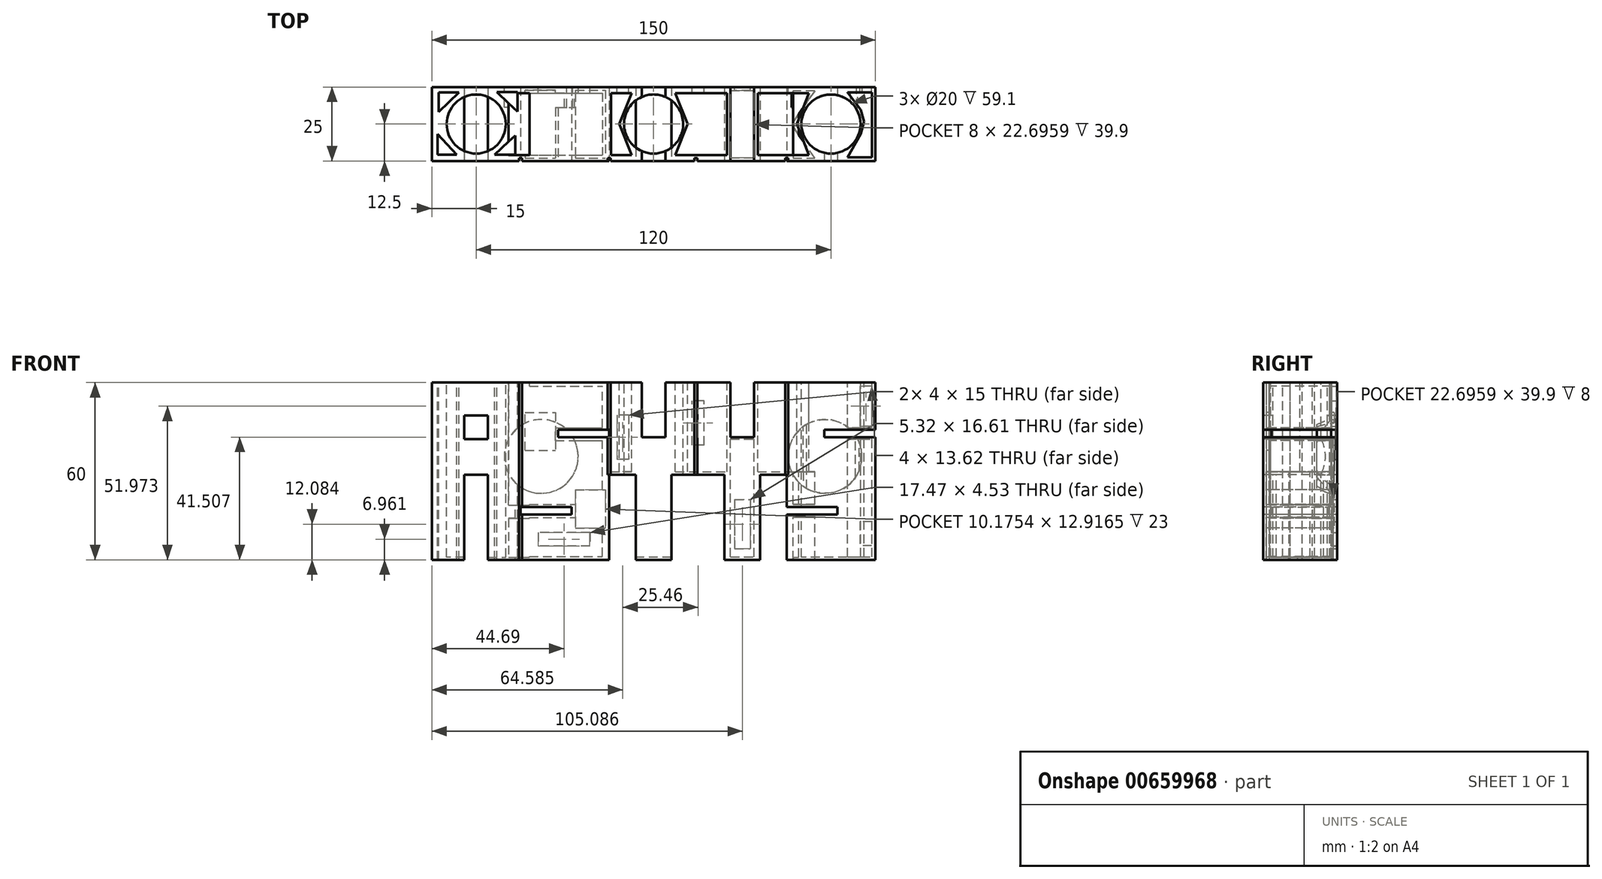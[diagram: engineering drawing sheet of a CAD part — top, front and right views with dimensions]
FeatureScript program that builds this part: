
annotation { "Feature Type Name" : "Feature", "Feature Type Description" : "" }
export const myFeature = defineFeature(function(context is Context, id is Id, definition is map)
    precondition{}
    {
        {
            var Q0;
            Q0=qCreatedBy(makeId("Front.planeOp"),FACE);
            var sketch = newSketch(context, id + "F0", { "sketchPlane" : qUnion([Q0])});
            skLineSegment(sketch, "E0.bottom", {"start": v(-75, 38.6) * mm, "end": v(75, 38.6) * mm});
            skLineSegment(sketch, "E0.top", {"start": v(-75, -21.4) * mm, "end": v(75, -21.4) * mm});
            skLineSegment(sketch, "E0.left", {"start": v(-75, 38.6) * mm, "end": v(-75, -21.4) * mm});
            skLineSegment(sketch, "E0.right", {"start": v(75, 38.6) * mm, "end": v(75, -21.4) * mm});
            skSolve(sketch);
        }
        {
            var Q0;
            Q0=qSketchRegion(id+"F0",true);
            extrude(context, id + "F1", {"entities" : qUnion([Q0]), "depth" : 25 * mm, "offsetDistance" : 25 * mm});
        }
        {
            var Q0;
            Q0=makeQuery(id+"F1.opExtrude","SWEPT_FACE",FACE,{"disambiguationData":[OSD([sQuery(id+"F0.wireOp",EDGE,"E0.bottom")])]});
            var sketch = newSketch(context, id + "F2", { "sketchPlane" : qUnion([Q0])});
            skLineSegment(sketch, "E1.bottom", {"start": v(-73, -2) * mm, "end": v(73, -2) * mm});
            skLineSegment(sketch, "E1.top", {"start": v(-73, -23) * mm, "end": v(73, -23) * mm});
            skLineSegment(sketch, "E1.left", {"start": v(-73, -2) * mm, "end": v(-73, -23) * mm});
            skLineSegment(sketch, "E1.right", {"start": v(73, -2) * mm, "end": v(73, -23) * mm});
            skLineSegment(sketch, "E2.MirrorCS", {"start": v(219, -2) * mm, "end": v(219, -23) * mm});
            skSolve(sketch);
        }
        {
            var Q0;
            Q0=qSketchRegion(id+"F2",true);
            extrude(context, id + "F3", {"entities" : qUnion([Q0]), "operationType" : NewBodyOperationType.ADD, "oppositeDirection" : true, "depth" : 2 * mm, "offsetDistance" : 25 * mm});
        }
        {
            var Q0;
            Q0=makeQuery(id+"F3.boolean.opBoolean","MERGE",FACE,{"derivedFrom":[makeQuery(id+"F1.opExtrude","SWEPT_FACE",FACE,{"disambiguationData":[OSD([sQuery(id+"F0.wireOp",EDGE,"E0.bottom")])]}),makeQuery(id+"F3.opExtrude","CAP_FACE",FACE,{"disambiguationData":[OSD([sQuery(id+"F2.wireOp",EDGE,"E1.bottom"),sQuery(id+"F2.wireOp",EDGE,"E1.top"),sQuery(id+"F2.wireOp",EDGE,"E1.left"),sQuery(id+"F2.wireOp",EDGE,"E1.right")])],"isStart":true})]});
            var sketch = newSketch(context, id + "F4", { "sketchPlane" : qUnion([Q0])});
            skCircle(sketch, "E3", {"center": v(60, -12.5) * mm, "radius": 10 * mm});
            skCircle(sketch, "E4.MirrorC", {"center": v(-60, -12.5) * mm, "radius": 10 * mm});
            skCircle(sketch, "E5", {"center": v(0, -12.5) * mm, "radius": 10 * mm});
            skSolve(sketch);
        }
        {
            var Q0;
            Q0=qSketchRegion(id+"F4",true);
            extrude(context, id + "F5", {"entities" : qUnion([Q0]), "operationType" : NewBodyOperationType.REMOVE, "oppositeDirection" : true, "depth" : 59.1 * mm, "offsetDistance" : 25 * mm});
        }
        {
            var Q0;
            Q0=makeQuery(id+"F1.opExtrude","CAP_FACE",FACE,{"disambiguationData":[OSD([sQuery(id+"F0.wireOp",EDGE,"E0.bottom"),sQuery(id+"F0.wireOp",EDGE,"E0.top"),sQuery(id+"F0.wireOp",EDGE,"E0.left"),sQuery(id+"F0.wireOp",EDGE,"E0.right")])],"isStart":true});
            var sketch = newSketch(context, id + "F6", { "sketchPlane" : qUnion([Q0])});
            skCircle(sketch, "E6", {"center": v(-58, 13.6) * mm, "radius": 12.5 * mm});
            skCircle(sketch, "E7.MirrorC", {"center": v(38, 13.6) * mm, "radius": 12.5 * mm});
            skSolve(sketch);
        }
        {
            var Q0;
            Q0=qSketchRegion(id+"F6",true);
            extrude(context, id + "F7", {"entities" : qUnion([Q0]), "operationType" : NewBodyOperationType.REMOVE, "oppositeDirection" : true, "depth" : 6.9 * mm, "offsetDistance" : 25 * mm});
        }
        {
            var Q0;
            Q0=makeQuery(id+"F1.opExtrude","CAP_FACE",FACE,{"disambiguationData":[OSD([sQuery(id+"F0.wireOp",EDGE,"E0.bottom"),sQuery(id+"F0.wireOp",EDGE,"E0.top"),sQuery(id+"F0.wireOp",EDGE,"E0.left"),sQuery(id+"F0.wireOp",EDGE,"E0.right")])],"isStart":false});
            var sketch = newSketch(context, id + "F8", { "sketchPlane" : qUnion([Q0])});
            skLineSegment(sketch, "E8.bottom", {"start": v(-75, 38.6) * mm, "end": v(-45, 38.6) * mm});
            skLineSegment(sketch, "E8.top", {"start": v(-75, -21.4) * mm, "end": v(-45, -21.4) * mm});
            skLineSegment(sketch, "E8.left", {"start": v(-75, 38.6) * mm, "end": v(-75, -21.4) * mm});
            skLineSegment(sketch, "E8.right", {"start": v(-45, 38.6) * mm, "end": v(-45, -21.4) * mm});
            skLineSegment(sketch, "E9", {"start": v(-60, 38.6) * mm, "end": v(-60, -21.4) * mm});
            skLineSegment(sketch, "E10", {"start": v(-64, -21.4) * mm, "end": v(-64, 7.4) * mm});
            skLineSegment(sketch, "E11", {"start": v(-64, 7.4) * mm, "end": v(-60, 7.4) * mm});
            skLineSegment(sketch, "E12", {"start": v(-60, 27.44) * mm, "end": v(-64, 27.44) * mm});
            skLineSegment(sketch, "E13", {"start": v(-64, 27.44) * mm, "end": v(-64, 19.44) * mm});
            skLineSegment(sketch, "E14", {"start": v(-64, 19.44) * mm, "end": v(-60, 19.44) * mm});
            skLineSegment(sketch, "E15.MirrorCS", {"start": v(-60, 27.44) * mm, "end": v(-56, 27.44) * mm});
            skLineSegment(sketch, "E16.MirrorCS", {"start": v(-56, 27.44) * mm, "end": v(-56, 19.44) * mm});
            skLineSegment(sketch, "E17.MirrorCS", {"start": v(-56, 19.44) * mm, "end": v(-60, 19.44) * mm});
            skLineSegment(sketch, "E18.MirrorCS", {"start": v(-56, 7.4) * mm, "end": v(-60, 7.4) * mm});
            skLineSegment(sketch, "E19.MirrorCS", {"start": v(-56, -21.4) * mm, "end": v(-56, 7.4) * mm});
            skLineSegment(sketch, "E20.bottom", {"start": v(-45, 38.6) * mm, "end": v(-15, 38.6) * mm});
            skLineSegment(sketch, "E20.top", {"start": v(-45, -21.4) * mm, "end": v(-15, -21.4) * mm});
            skLineSegment(sketch, "E20.right", {"start": v(-15, 38.6) * mm, "end": v(-15, -21.4) * mm});
            skLineSegment(sketch, "E21.bottom", {"start": v(-15, 20.1) * mm, "end": v(-32.25, 20.1) * mm});
            skLineSegment(sketch, "E21.top", {"start": v(-15, 22.68) * mm, "end": v(-32.25, 22.68) * mm});
            skLineSegment(sketch, "E21.left", {"start": v(-15, 22.68) * mm, "end": v(-15, 20.1) * mm});
            skLineSegment(sketch, "E21.right", {"start": v(-32.25, 22.68) * mm, "end": v(-32.25, 20.1) * mm});
            skLineSegment(sketch, "E22.bottom", {"start": v(-45, -3.49) * mm, "end": v(-27.75, -3.49) * mm});
            skLineSegment(sketch, "E22.top", {"start": v(-45, -6.06) * mm, "end": v(-27.75, -6.06) * mm});
            skLineSegment(sketch, "E22.left", {"start": v(-45, -3.49) * mm, "end": v(-45, -6.06) * mm});
            skLineSegment(sketch, "E22.right", {"start": v(-27.75, -3.49) * mm, "end": v(-27.75, -6.06) * mm});
            skLineSegment(sketch, "E23.bottom", {"start": v(-15, 38.6) * mm, "end": v(15, 38.6) * mm});
            skLineSegment(sketch, "E23.top", {"start": v(-15, -21.4) * mm, "end": v(15, -21.4) * mm});
            skLineSegment(sketch, "E23.right", {"start": v(15, 38.6) * mm, "end": v(15, -21.4) * mm});
            skLineSegment(sketch, "E24", {"start": v(-4, 38.6) * mm, "end": v(-4, 20.1) * mm});
            skLineSegment(sketch, "E25", {"start": v(-4, 20.1) * mm, "end": v(0, 20.1) * mm});
            skLineSegment(sketch, "E26.MirrorCS", {"start": v(4, 38.6) * mm, "end": v(4, 20.1) * mm});
            skLineSegment(sketch, "E27.MirrorCS", {"start": v(4, 20.1) * mm, "end": v(0, 20.1) * mm});
            skLineSegment(sketch, "E28", {"start": v(-15, 7.4) * mm, "end": v(-6, 7.4) * mm});
            skLineSegment(sketch, "E29", {"start": v(-6, 7.4) * mm, "end": v(-6, -21.4) * mm});
            skLineSegment(sketch, "E30.bottom", {"start": v(15, 38.6) * mm, "end": v(45, 38.6) * mm});
            skLineSegment(sketch, "E30.top", {"start": v(15, -21.4) * mm, "end": v(45, -21.4) * mm});
            skLineSegment(sketch, "E30.right", {"start": v(45, 38.6) * mm, "end": v(45, -21.4) * mm});
            skLineSegment(sketch, "E31", {"start": v(30, 38.6) * mm, "end": v(30, -21.4) * mm});
            skLineSegment(sketch, "E32", {"start": v(26, 20.1) * mm, "end": v(30, 20.1) * mm});
            skLineSegment(sketch, "E33", {"start": v(26, 20.1) * mm, "end": v(26, 38.6) * mm});
            skLineSegment(sketch, "E34.MirrorCS", {"start": v(34, 20.1) * mm, "end": v(34, 38.6) * mm});
            skLineSegment(sketch, "E35.MirrorCS", {"start": v(34, 20.1) * mm, "end": v(30, 20.1) * mm});
            skLineSegment(sketch, "E36", {"start": v(15, 7.4) * mm, "end": v(24, 7.4) * mm});
            skLineSegment(sketch, "E37", {"start": v(24, 7.4) * mm, "end": v(24, -21.4) * mm});
            skLineSegment(sketch, "E38.MirrorCS", {"start": v(45, 7.4) * mm, "end": v(36, 7.4) * mm});
            skLineSegment(sketch, "E39.MirrorCS", {"start": v(36, 7.4) * mm, "end": v(36, -21.4) * mm});
            skLineSegment(sketch, "E40.MirrorCS", {"start": v(6, 7.4) * mm, "end": v(6, -21.4) * mm});
            skLineSegment(sketch, "E41", {"start": v(6, 7.4) * mm, "end": v(15, 7.4) * mm});
            skLineSegment(sketch, "E42", {"start": v(57.75, 22.68) * mm, "end": v(75, 22.68) * mm});
            skLineSegment(sketch, "E43", {"start": v(57.75, 20.1) * mm, "end": v(75, 20.1) * mm});
            skPoint(sketch, "E43.startSnap0", {"position": v(32, 20.1) * mm});
            skLineSegment(sketch, "E44", {"start": v(57.75, 22.68) * mm, "end": v(57.75, 20.1) * mm});
            skLineSegment(sketch, "E45", {"start": v(45, -3.49) * mm, "end": v(62.25, -3.49) * mm});
            skLineSegment(sketch, "E46", {"start": v(62.25, -3.49) * mm, "end": v(62.25, -6.06) * mm});
            skLineSegment(sketch, "E47", {"start": v(62.25, -6.06) * mm, "end": v(45, -6.06) * mm});
            skSolve(sketch);
        }
        {
            var Q0;
            {var subQ0=sQuery(id+"F8.wireOp",EDGE,"E12");Q0=makeQuery(id+"F8.imprint","IMPRINT",FACE,{"disambiguationData":[TD([[makeQuery(id+"F8.imprint","IMPRINT",EDGE,{"derivedFrom":subQ0}),1.0]])]});}
            var Q1;
            {var subQ0=sQuery(id+"F8.wireOp",EDGE,"E15.MirrorCS");Q1=makeQuery(id+"F8.imprint","IMPRINT",FACE,{"disambiguationData":[TD([[makeQuery(id+"F8.imprint","IMPRINT",EDGE,{"derivedFrom":subQ0}),-1.0]])]});}
            var Q2;
            {var subQ3=sQuery(id+"F8.wireOp",EDGE,"E10");Q2=makeQuery(id+"F8.imprint","IMPRINT",FACE,{"disambiguationData":[TD([[makeQuery(id+"F8.imprint","IMPRINT",EDGE,{"derivedFrom":subQ3}),-1.0]])]});}
            var Q3;
            {var subQ4=sQuery(id+"F8.wireOp",EDGE,"E18.MirrorCS");Q3=makeQuery(id+"F8.imprint","IMPRINT",FACE,{"disambiguationData":[TD([[makeQuery(id+"F8.imprint","IMPRINT",EDGE,{"derivedFrom":subQ4}),1.0]])]});}
            var Q4;
            Q4=makeQuery(id+"F8.imprint","IMPRINT",FACE,{"disambiguationData":[TD([[makeQuery(id+"F8.imprint","IMPRINT",EDGE,{"derivedFrom":sQuery(id+"F8.wireOp",EDGE,"E22.bottom")}),-1.0]])]});
            var Q5;
            {var subQ0=sQuery(id+"F8.wireOp",EDGE,"E21.bottom");Q5=makeQuery(id+"F8.imprint","IMPRINT",FACE,{"disambiguationData":[TD([[makeQuery(id+"F8.imprint","IMPRINT",EDGE,{"derivedFrom":subQ0}),-1.0]])]});}
            var Q6;
            {var subQ1=sQuery(id+"F8.wireOp",EDGE,"E24");Q6=makeQuery(id+"F8.imprint","IMPRINT",FACE,{"disambiguationData":[TD([[makeQuery(id+"F8.imprint","IMPRINT",EDGE,{"derivedFrom":subQ1}),1.0]])]});}
            var Q7;
            {var subQ4=sQuery(id+"F8.wireOp",EDGE,"E28");Q7=makeQuery(id+"F8.imprint","IMPRINT",FACE,{"disambiguationData":[TD([[makeQuery(id+"F8.imprint","IMPRINT",EDGE,{"derivedFrom":subQ4}),-1.0]])]});}
            var Q8;
            {var subQ3=sQuery(id+"F8.wireOp",EDGE,"E40.MirrorCS");Q8=makeQuery(id+"F8.imprint","IMPRINT",FACE,{"disambiguationData":[TD([[makeQuery(id+"F8.imprint","IMPRINT",EDGE,{"derivedFrom":subQ3}),1.0]])]});}
            var Q9;
            {var subQ4=sQuery(id+"F8.wireOp",EDGE,"E36");Q9=makeQuery(id+"F8.imprint","IMPRINT",FACE,{"disambiguationData":[TD([[makeQuery(id+"F8.imprint","IMPRINT",EDGE,{"derivedFrom":subQ4}),-1.0]])]});}
            var Q10;
            {var subQ3=sQuery(id+"F8.wireOp",EDGE,"E34.MirrorCS");Q10=makeQuery(id+"F8.imprint","IMPRINT",FACE,{"disambiguationData":[TD([[makeQuery(id+"F8.imprint","IMPRINT",EDGE,{"derivedFrom":subQ3}),1.0]])]});}
            var Q11;
            {var subQ4=sQuery(id+"F8.wireOp",EDGE,"E32");Q11=makeQuery(id+"F8.imprint","IMPRINT",FACE,{"disambiguationData":[TD([[makeQuery(id+"F8.imprint","IMPRINT",EDGE,{"derivedFrom":subQ4}),1.0]])]});}
            var Q12;
            {var subQ4=sQuery(id+"F8.wireOp",EDGE,"E38.MirrorCS");Q12=makeQuery(id+"F8.imprint","IMPRINT",FACE,{"disambiguationData":[TD([[makeQuery(id+"F8.imprint","IMPRINT",EDGE,{"derivedFrom":subQ4}),1.0]])]});}
            var Q13;
            {var subQ0=sQuery(id+"F8.wireOp",EDGE,"E45");Q13=makeQuery(id+"F8.imprint","IMPRINT",FACE,{"disambiguationData":[TD([[makeQuery(id+"F8.imprint","IMPRINT",EDGE,{"derivedFrom":subQ0}),-1.0]])]});}
            var Q14;
            {var subQ0=sQuery(id+"F8.wireOp",EDGE,"E42");Q14=makeQuery(id+"F8.imprint","IMPRINT",FACE,{"disambiguationData":[TD([[makeQuery(id+"F8.imprint","IMPRINT",EDGE,{"derivedFrom":subQ0}),-1.0]])]});}
            extrude(context, id + "F9", {"entities" : qUnion([Q0, Q1, Q2, Q3, Q4, Q5, Q6, Q7, Q8, Q9, Q10, Q11, Q12, Q13, Q14]), "operationType" : NewBodyOperationType.REMOVE, "oppositeDirection" : true, "depth" : 35.6 * mm, "offsetDistance" : 25 * mm});
        }
        {
            var Q0;
            Q0=makeQuery(id+"F1.opExtrude","CAP_FACE",FACE,{"disambiguationData":[OSD([sQuery(id+"F0.wireOp",EDGE,"E0.bottom"),sQuery(id+"F0.wireOp",EDGE,"E0.top"),sQuery(id+"F0.wireOp",EDGE,"E0.left"),sQuery(id+"F0.wireOp",EDGE,"E0.right")])],"isStart":false});
            var sketch = newSketch(context, id + "F10", { "sketchPlane" : qUnion([Q0])});
            skPoint(sketch, "E48.oppositeSnap0", {"position": v(-45, -4.78) * mm});
            skLineSegment(sketch, "E48.bottom", {"start": v(-75, 38.6) * mm, "end": v(-45, 38.6) * mm});
            skLineSegment(sketch, "E48.top", {"start": v(-75, -21.4) * mm, "end": v(-45, -21.4) * mm});
            skLineSegment(sketch, "E48.left", {"start": v(-75, 38.6) * mm, "end": v(-75, -21.4) * mm});
            skLineSegment(sketch, "E48.right", {"start": v(-45, 38.6) * mm, "end": v(-45, -21.4) * mm});
            skLineSegment(sketch, "E49.bottom", {"start": v(-45, 38.6) * mm, "end": v(-15, 38.6) * mm});
            skLineSegment(sketch, "E49.top", {"start": v(-45, -21.4) * mm, "end": v(-15, -21.4) * mm});
            skLineSegment(sketch, "E49.right", {"start": v(-15, 38.6) * mm, "end": v(-15, -21.4) * mm});
            skLineSegment(sketch, "E50.bottom", {"start": v(-15, 38.6) * mm, "end": v(14.35, 38.6) * mm});
            skLineSegment(sketch, "E50.top", {"start": v(-15, -21.4) * mm, "end": v(14.35, -21.4) * mm});
            skLineSegment(sketch, "E50.right", {"start": v(14.35, 38.6) * mm, "end": v(14.35, -21.4) * mm});
            skLineSegment(sketch, "E51.bottom", {"start": v(14.35, 38.6) * mm, "end": v(45, 38.6) * mm});
            skLineSegment(sketch, "E51.top", {"start": v(14.35, -21.4) * mm, "end": v(45, -21.4) * mm});
            skLineSegment(sketch, "E51.right", {"start": v(45, 38.6) * mm, "end": v(45, -21.4) * mm});
            skLineSegment(sketch, "E52", {"start": v(-45.5, 38.6) * mm, "end": v(-45.5, -21.4) * mm});
            skLineSegment(sketch, "E53.MirrorCS", {"start": v(-44.5, 38.6) * mm, "end": v(-44.5, -21.4) * mm});
            skLineSegment(sketch, "E54", {"start": v(-14.5, 38.6) * mm, "end": v(-14.5, 7.4) * mm});
            skLineSegment(sketch, "E55", {"start": v(13.85, 38.6) * mm, "end": v(13.85, 7.4) * mm});
            skLineSegment(sketch, "E56.MirrorCS", {"start": v(14.85, 38.6) * mm, "end": v(14.85, 7.4) * mm});
            skLineSegment(sketch, "E57", {"start": v(44.5, 38.6) * mm, "end": v(44.5, 7.4) * mm});
            skLineSegment(sketch, "E58.MirrorCS", {"start": v(-15.5, 38.6) * mm, "end": v(-15.5, 7.4) * mm});
            skLineSegment(sketch, "E59", {"start": v(-15.5, 7.4) * mm, "end": v(-15, 7.4) * mm});
            skLineSegment(sketch, "E60.MirrorCS", {"start": v(45.5, 38.6) * mm, "end": v(45.5, 7.4) * mm});
            skLineSegment(sketch, "E61", {"start": v(45, 7.4) * mm, "end": v(45.5, 7.4) * mm});
            skSolve(sketch);
        }
        {
            var Q0;
            {var subQ1=makeQuery(id+"F9.boolean.opBoolean","COPY",EDGE,{"derivedFrom":makeQuery(id+"F9.opExtrude","CAP_EDGE",EDGE,{"disambiguationData":[OSD([sQuery(id+"F8.wireOp",EDGE,"E10")])],"isStart":true})});Q0=makeQuery(id+"F10.imprint","IMPRINT",FACE,{"disambiguationData":[TD([[makeQuery(id+"F10.imprint","IMPRINT",EDGE,{"derivedFrom":subQ1}),-1.0]])]});}
            var Q1;
            {var subQ1=makeQuery(id+"F9.boolean.opBoolean","COPY",EDGE,{"derivedFrom":makeQuery(id+"F9.opExtrude","CAP_EDGE",EDGE,{"disambiguationData":[OSD([sQuery(id+"F8.wireOp",EDGE,"E24")])],"isStart":true})});Q1=makeQuery(id+"F10.imprint","IMPRINT",FACE,{"disambiguationData":[TD([[makeQuery(id+"F10.imprint","IMPRINT",EDGE,{"derivedFrom":subQ1}),1.0]])]});}
            var Q2;
            {var subQ1=makeQuery(id+"F9.boolean.opBoolean","COPY",EDGE,{"derivedFrom":makeQuery(id+"F9.opExtrude","CAP_EDGE",EDGE,{"disambiguationData":[OSD([sQuery(id+"F8.wireOp",EDGE,"E33")])],"isStart":true})});Q2=makeQuery(id+"F10.imprint","IMPRINT",FACE,{"disambiguationData":[TD([[makeQuery(id+"F10.imprint","IMPRINT",EDGE,{"derivedFrom":subQ1}),-1.0]])]});}
            var Q3;
            Q3=makeQuery(id+"F10.imprint","IMPRINT",FACE,{"disambiguationData":[TD([[makeQuery(id+"F10.imprint","IMPRINT",EDGE,{"derivedFrom":makeQuery(id+"F9.boolean.opBoolean","COPY",EDGE,{"derivedFrom":makeQuery(id+"F9.opExtrude","CAP_EDGE",EDGE,{"disambiguationData":[OSD([sQuery(id+"F8.wireOp",EDGE,"E13")])],"isStart":true})})}),1.0]])]});
            var Q4;
            {var subQ1=sQuery(id+"F10.wireOp",EDGE,"E49.top");var subQ3=sQuery(id+"F10.wireOp",EDGE,"E53.MirrorCS");var subQ4=makeQuery(id+"F10.imprint","INTERSECT",VERTEX,{"derivedFrom":[subQ1,subQ3]});Q4=makeQuery(id+"F10.imprint","IMPRINT",FACE,{"disambiguationData":[TD([[makeQuery(id+"F10.imprint","IMPRINT",EDGE,{"disambiguationData":[TD([[subQ4,1.0]])],"derivedFrom":subQ3}),-1.0]])]});}
            var Q5;
            {var subQ5=makeQuery(id+"F9.boolean.opBoolean","COPY",EDGE,{"derivedFrom":makeQuery(id+"F9.opExtrude","CAP_EDGE",EDGE,{"disambiguationData":[OSD([sQuery(id+"F8.wireOp",EDGE,"E22.right")])],"isStart":true})});Q5=makeQuery(id+"F10.imprint","IMPRINT",FACE,{"disambiguationData":[TD([[makeQuery(id+"F10.imprint","IMPRINT",EDGE,{"derivedFrom":subQ5}),-1.0]])]});}
            var Q6;
            {var subQ5=makeQuery(id+"F9.boolean.opBoolean","COPY",EDGE,{"derivedFrom":makeQuery(id+"F9.opExtrude","CAP_EDGE",EDGE,{"disambiguationData":[OSD([sQuery(id+"F8.wireOp",EDGE,"E21.right")])],"isStart":true})});Q6=makeQuery(id+"F10.imprint","IMPRINT",FACE,{"disambiguationData":[TD([[makeQuery(id+"F10.imprint","IMPRINT",EDGE,{"derivedFrom":subQ5}),1.0]])]});}
            var Q7;
            {var subQ0=makeQuery(id+"F9.boolean.opBoolean","COPY",EDGE,{"derivedFrom":makeQuery(id+"F9.opExtrude","CAP_EDGE",EDGE,{"disambiguationData":[OSD([sQuery(id+"F8.wireOp",EDGE,"E29")])],"isStart":true})});Q7=makeQuery(id+"F10.imprint","IMPRINT",FACE,{"disambiguationData":[TD([[makeQuery(id+"F10.imprint","IMPRINT",EDGE,{"derivedFrom":subQ0}),-1.0]])]});}
            var Q8;
            {var subQ0=makeQuery(id+"F9.boolean.opBoolean","COPY",EDGE,{"derivedFrom":makeQuery(id+"F9.opExtrude","CAP_EDGE",EDGE,{"disambiguationData":[OSD([sQuery(id+"F8.wireOp",EDGE,"E40.MirrorCS")])],"isStart":true})});Q8=makeQuery(id+"F10.imprint","IMPRINT",FACE,{"disambiguationData":[TD([[makeQuery(id+"F10.imprint","IMPRINT",EDGE,{"derivedFrom":subQ0}),1.0]])]});}
            var Q9;
            {var subQ0=makeQuery(id+"F9.boolean.opBoolean","COPY",EDGE,{"derivedFrom":makeQuery(id+"F9.opExtrude","CAP_EDGE",EDGE,{"disambiguationData":[OSD([sQuery(id+"F8.wireOp",EDGE,"E37")])],"isStart":true})});Q9=makeQuery(id+"F10.imprint","IMPRINT",FACE,{"disambiguationData":[TD([[makeQuery(id+"F10.imprint","IMPRINT",EDGE,{"derivedFrom":subQ0}),-1.0]])]});}
            var Q10;
            {var subQ0=sQuery(id+"F10.wireOp",EDGE,"E48.right");var subQ1=makeQuery(id+"F9.boolean.opBoolean","COPY",EDGE,{"derivedFrom":makeQuery(id+"F9.opExtrude","CAP_EDGE",EDGE,{"disambiguationData":[OSD([sQuery(id+"F8.wireOp",EDGE,"E22.bottom")])],"isStart":true})});var subQ2=makeQuery(id+"F10.imprint","INTERSECT",VERTEX,{"derivedFrom":[subQ1,subQ0]});Q10=makeQuery(id+"F10.imprint","IMPRINT",FACE,{"disambiguationData":[TD([[makeQuery(id+"F10.imprint","IMPRINT",EDGE,{"disambiguationData":[TD([[subQ2,-1.0]])],"derivedFrom":subQ0}),1.0]])]});}
            var Q11;
            {var subQ10=makeQuery(id+"F9.boolean.opBoolean","COPY",EDGE,{"derivedFrom":makeQuery(id+"F9.opExtrude","CAP_EDGE",EDGE,{"disambiguationData":[OSD([sQuery(id+"F8.wireOp",EDGE,"E39.MirrorCS")])],"isStart":true})});Q11=makeQuery(id+"F10.imprint","IMPRINT",FACE,{"disambiguationData":[TD([[makeQuery(id+"F10.imprint","IMPRINT",EDGE,{"derivedFrom":subQ10}),1.0]])]});}
            var Q12;
            {var subQ6=sQuery(id+"F10.wireOp",EDGE,"E60.MirrorCS");Q12=makeQuery(id+"F10.imprint","IMPRINT",FACE,{"disambiguationData":[TD([[makeQuery(id+"F10.imprint","IMPRINT",EDGE,{"derivedFrom":subQ6}),-1.0]])]});}
            var Q13;
            {var subQ5=sQuery(id+"F10.wireOp",EDGE,"E57");Q13=makeQuery(id+"F10.imprint","IMPRINT",FACE,{"disambiguationData":[TD([[makeQuery(id+"F10.imprint","IMPRINT",EDGE,{"derivedFrom":subQ5}),1.0]])]});}
            var Q14;
            {var subQ3=sQuery(id+"F10.wireOp",EDGE,"E56.MirrorCS");Q14=makeQuery(id+"F10.imprint","IMPRINT",FACE,{"disambiguationData":[TD([[makeQuery(id+"F10.imprint","IMPRINT",EDGE,{"derivedFrom":subQ3}),-1.0]])]});}
            var Q15;
            {var subQ3=sQuery(id+"F10.wireOp",EDGE,"E55");Q15=makeQuery(id+"F10.imprint","IMPRINT",FACE,{"disambiguationData":[TD([[makeQuery(id+"F10.imprint","IMPRINT",EDGE,{"derivedFrom":subQ3}),1.0]])]});}
            var Q16;
            {var subQ5=sQuery(id+"F10.wireOp",EDGE,"E54");Q16=makeQuery(id+"F10.imprint","IMPRINT",FACE,{"disambiguationData":[TD([[makeQuery(id+"F10.imprint","IMPRINT",EDGE,{"derivedFrom":subQ5}),-1.0]])]});}
            var Q17;
            {var subQ1=sQuery(id+"F10.wireOp",EDGE,"E49.bottom");var subQ3=sQuery(id+"F10.wireOp",EDGE,"E58.MirrorCS");var subQ4=makeQuery(id+"F10.imprint","INTERSECT",VERTEX,{"derivedFrom":[subQ1,subQ3]});Q17=makeQuery(id+"F10.imprint","IMPRINT",FACE,{"disambiguationData":[TD([[makeQuery(id+"F10.imprint","IMPRINT",EDGE,{"disambiguationData":[TD([[subQ4,-1.0]])],"derivedFrom":subQ3}),1.0]])]});}
            var Q18;
            {var subQ3=sQuery(id+"F10.wireOp",EDGE,"E59");Q18=makeQuery(id+"F10.imprint","IMPRINT",FACE,{"disambiguationData":[TD([[makeQuery(id+"F10.imprint","IMPRINT",EDGE,{"derivedFrom":subQ3}),1.0]])]});}
            var Q19;
            {var subQ0=sQuery(id+"F10.wireOp",EDGE,"E49.right");var subQ1=makeQuery(id+"F9.boolean.opBoolean","COPY",EDGE,{"derivedFrom":makeQuery(id+"F9.opExtrude","CAP_EDGE",EDGE,{"disambiguationData":[OSD([sQuery(id+"F8.wireOp",EDGE,"E21.bottom")])],"isStart":true})});var subQ2=makeQuery(id+"F10.imprint","INTERSECT",VERTEX,{"derivedFrom":[subQ1,subQ0]});Q19=makeQuery(id+"F10.imprint","IMPRINT",FACE,{"disambiguationData":[TD([[makeQuery(id+"F10.imprint","IMPRINT",EDGE,{"disambiguationData":[TD([[subQ2,1.0]])],"derivedFrom":subQ0}),-1.0]])]});}
            var Q20;
            {var subQ1=sQuery(id+"F10.wireOp",EDGE,"E49.bottom");var subQ3=sQuery(id+"F10.wireOp",EDGE,"E53.MirrorCS");var subQ4=makeQuery(id+"F10.imprint","INTERSECT",VERTEX,{"derivedFrom":[subQ1,subQ3]});Q20=makeQuery(id+"F10.imprint","IMPRINT",FACE,{"disambiguationData":[TD([[makeQuery(id+"F10.imprint","IMPRINT",EDGE,{"disambiguationData":[TD([[subQ4,-1.0]])],"derivedFrom":subQ3}),-1.0]])]});}
            var Q21;
            {var subQ5=sQuery(id+"F10.wireOp",EDGE,"E52");Q21=makeQuery(id+"F10.imprint","IMPRINT",FACE,{"disambiguationData":[TD([[makeQuery(id+"F10.imprint","IMPRINT",EDGE,{"derivedFrom":subQ5}),1.0]])]});}
            extrude(context, id + "F11", {"entities" : qUnion([Q0, Q1, Q2, Q3, Q4, Q5, Q6, Q7, Q8, Q9, Q10, Q11, Q12, Q13, Q14, Q15, Q16, Q17, Q18, Q19, Q20, Q21]), "operationType" : NewBodyOperationType.REMOVE, "oppositeDirection" : true, "depth" : 1 * mm, "offsetDistance" : 25 * mm});
        }
        {
            var Q0;
            {var subQ0=sQuery(id+"F0.wireOp",EDGE,"E0.left");var subQ3=sQuery(id+"F0.wireOp",EDGE,"E0.bottom");Q0=makeQuery(id+"F9.boolean.opBoolean","SPLIT",FACE,{"disambiguationData":[TD([makeQuery(id+"F1.opExtrude","SWEPT_FACE",FACE,{"disambiguationData":[OSD([subQ0])]})])],"derivedFrom":makeQuery(id+"F1.opExtrude","SWEPT_FACE",FACE,{"disambiguationData":[OSD([subQ3])]})});}
            var sketch = newSketch(context, id + "F12", { "sketchPlane" : qUnion([Q0])});
            skLineSegment(sketch, "E62.bottom", {"start": v(-42.02, -2) * mm, "end": v(-17.36, -2) * mm});
            skLineSegment(sketch, "E62.top", {"start": v(-42.02, -23) * mm, "end": v(-17.36, -23) * mm});
            skLineSegment(sketch, "E62.left", {"start": v(-42.02, -2) * mm, "end": v(-42.02, -23) * mm});
            skLineSegment(sketch, "E62.right", {"start": v(-17.36, -2) * mm, "end": v(-17.36, -23) * mm});
            skSolve(sketch);
        }
        {
            var Q0;
            Q0=makeQuery(id+"F12.imprint","IMPRINT",FACE,{"disambiguationData":[TD([[makeQuery(id+"F12.imprint","IMPRINT",EDGE,{"derivedFrom":sQuery(id+"F12.wireOp",EDGE,"E62.bottom")}),-1.0]])]});
            extrude(context, id + "F13", {"entities" : qUnion([Q0]), "operationType" : NewBodyOperationType.REMOVE, "oppositeDirection" : true, "depth" : 15.3 * mm, "offsetDistance" : 25 * mm, "hasSecondDirection" : true, "secondDirectionOppositeDirection" : true, "secondDirectionDepth" : 1.3 * mm});
        }
        {
            var Q0;
            Q0 = qSketchRegion(id + "F12", true);
            extrude(context, id + "F14", {"entities" : qUnion([Q0]), "operationType" : NewBodyOperationType.REMOVE, "oppositeDirection" : true, "depth" : 41.3 * mm, "offsetDistance" : 25 * mm, "hasSecondDirection" : true, "secondDirectionOppositeDirection" : true, "secondDirectionDepth" : 19.6 * mm});
        }
        {
            var Q0;
            Q0 = qSketchRegion(id + "F12", true);
            extrude(context, id + "F15", {"entities" : qUnion([Q0]), "operationType" : NewBodyOperationType.REMOVE, "oppositeDirection" : true, "depth" : 58.9 * mm, "offsetDistance" : 25 * mm, "hasSecondDirection" : true, "secondDirectionOppositeDirection" : true, "secondDirectionDepth" : 45.7 * mm});
        }
        {
            var Q0;
            {var subQ5=sQuery(id+"F0.wireOp",EDGE,"E0.bottom");var subQ6=sQuery(id+"F8.wireOp",EDGE,"E21.bottom");var subQ7=sQuery(id+"F0.wireOp",EDGE,"E0.top");Q0=makeQuery(id+"F11.boolean.opBoolean","SPLIT",FACE,{"disambiguationData":[TD([makeQuery(id+"F9.boolean.opBoolean","COPY",FACE,{"derivedFrom":makeQuery(id+"F9.opExtrude","SWEPT_FACE",FACE,{"disambiguationData":[OSD([subQ6])]})})])],"derivedFrom":makeQuery(id+"F1.opExtrude","CAP_FACE",FACE,{"disambiguationData":[OSD([subQ5,subQ7,sQuery(id+"F0.wireOp",EDGE,"E0.left"),sQuery(id+"F0.wireOp",EDGE,"E0.right")])],"isStart":false})});}
            var sketch = newSketch(context, id + "F16", { "sketchPlane" : qUnion([Q0])});
            skLineSegment(sketch, "E63.bottom", {"start": v(-26.47, 2.34) * mm, "end": v(-16.29, 2.34) * mm});
            skLineSegment(sketch, "E63.top", {"start": v(-26.47, -10.58) * mm, "end": v(-16.29, -10.58) * mm});
            skLineSegment(sketch, "E63.left", {"start": v(-26.47, 2.34) * mm, "end": v(-26.47, -10.58) * mm});
            skLineSegment(sketch, "E63.right", {"start": v(-16.29, 2.34) * mm, "end": v(-16.29, -10.58) * mm});
            skLineSegment(sketch, "E64.bottom", {"start": v(-43.43, 28.52) * mm, "end": v(-33.25, 28.52) * mm});
            skLineSegment(sketch, "E64.top", {"start": v(-43.43, 15.6) * mm, "end": v(-33.25, 15.6) * mm});
            skLineSegment(sketch, "E64.left", {"start": v(-43.43, 28.52) * mm, "end": v(-43.43, 15.6) * mm});
            skLineSegment(sketch, "E64.right", {"start": v(-33.25, 28.52) * mm, "end": v(-33.25, 15.6) * mm});
            skSolve(sketch);
        }
        {
            var Q0;
            Q0 = qSketchRegion(id + "F16", true);
            extrude(context, id + "F17", {"entities" : qUnion([Q0]), "operationType" : NewBodyOperationType.REMOVE, "oppositeDirection" : true, "depth" : 24 * mm, "offsetDistance" : 25 * mm, "hasSecondDirection" : true, "secondDirectionOppositeDirection" : true, "secondDirectionDepth" : 1 * mm});
        }
        {
            var Q0;
            {var subQ0=sQuery(id+"F0.wireOp",EDGE,"E0.left");var subQ3=sQuery(id+"F0.wireOp",EDGE,"E0.bottom");Q0=makeQuery(id+"F9.boolean.opBoolean","SPLIT",FACE,{"disambiguationData":[TD([makeQuery(id+"F1.opExtrude","SWEPT_FACE",FACE,{"disambiguationData":[OSD([subQ0])]})])],"derivedFrom":makeQuery(id+"F1.opExtrude","SWEPT_FACE",FACE,{"disambiguationData":[OSD([subQ3])]})});}
            var sketch = newSketch(context, id + "F18", { "sketchPlane" : qUnion([Q0])});
            skLineSegment(sketch, "E65.bottom", {"start": v(-49.03, -2) * mm, "end": v(-42.02, -2) * mm});
            skLineSegment(sketch, "E65.top", {"start": v(-49.03, -23) * mm, "end": v(-42.02, -23) * mm});
            skLineSegment(sketch, "E65.left", {"start": v(-49.03, -2) * mm, "end": v(-49.03, -23) * mm});
            skLineSegment(sketch, "E65.right", {"start": v(-42.02, -2) * mm, "end": v(-42.02, -23) * mm});
            skSolve(sketch);
        }
        {
            var Q0;
            Q0 = qSketchRegion(id + "F18", true);
            extrude(context, id + "F19", {"entities" : qUnion([Q0]), "operationType" : NewBodyOperationType.REMOVE, "oppositeDirection" : true, "depth" : 41.5 * mm, "offsetDistance" : 25 * mm, "hasSecondDirection" : true, "secondDirectionOppositeDirection" : true, "secondDirectionDepth" : 8E-4000 * mm});
        }
        {
            var Q0;
            Q0 = qSketchRegion(id + "F18", true);
            extrude(context, id + "F20", {"entities" : qUnion([Q0]), "operationType" : NewBodyOperationType.REMOVE, "oppositeDirection" : true, "depth" : 59.19 * mm, "offsetDistance" : 25 * mm, "hasSecondDirection" : true, "secondDirectionOppositeDirection" : true, "secondDirectionDepth" : 46 * mm});
        }
        {
            var Q0;
            Q0=makeQuery(id+"F12.imprint","IMPRINT",FACE,{"disambiguationData":[TD([[makeQuery(id+"F12.imprint","IMPRINT",EDGE,{"derivedFrom":sQuery(id+"F12.wireOp",EDGE,"E62.bottom")}),1.0]])]});
            var sketch = newSketch(context, id + "F21", { "sketchPlane" : qUnion([Q0])});
            skLineSegment(sketch, "E66", {"start": v(-72.75, -1.84) * mm, "end": v(-65.84, -1.84) * mm});
            skLineSegment(sketch, "E67", {"start": v(-65.84, -1.84) * mm, "end": v(-72.75, -8.37) * mm});
            skLineSegment(sketch, "E68", {"start": v(-72.75, -8.37) * mm, "end": v(-72.75, -1.84) * mm});
            skLineSegment(sketch, "E69", {"start": v(-73.08, -22.83) * mm, "end": v(-73.08, -15.91) * mm});
            skLineSegment(sketch, "E70", {"start": v(-73.08, -15.91) * mm, "end": v(-66.56, -22.83) * mm});
            skLineSegment(sketch, "E71", {"start": v(-66.56, -22.83) * mm, "end": v(-73.08, -22.83) * mm});
            skLineSegment(sketch, "E72", {"start": v(-46.81, -22.9) * mm, "end": v(-53.73, -22.9) * mm});
            skLineSegment(sketch, "E73", {"start": v(-53.73, -22.9) * mm, "end": v(-46.81, -16.37) * mm});
            skLineSegment(sketch, "E74", {"start": v(-46.81, -16.37) * mm, "end": v(-46.81, -22.9) * mm});
            skLineSegment(sketch, "E75.MirrorCS", {"start": v(-46.07, -1.7) * mm, "end": v(-53, -1.7) * mm});
            skLineSegment(sketch, "E76.MirrorCS", {"start": v(-53, -1.7) * mm, "end": v(-46.07, -8.22) * mm});
            skLineSegment(sketch, "E77.MirrorCS", {"start": v(-46.07, -8.22) * mm, "end": v(-46.07, -1.7) * mm});
            skSolve(sketch);
        }
        {
            var Q0;
            Q0 = qSketchRegion(id + "F21", true);
            extrude(context, id + "F22", {"entities" : qUnion([Q0]), "operationType" : NewBodyOperationType.REMOVE, "oppositeDirection" : true, "depth" : 60.8 * mm, "offsetDistance" : 25 * mm, "hasSecondDirection" : true, "secondDirectionOppositeDirection" : true, "secondDirectionDepth" : 9E-4000 * mm});
        }
        {
            var Q0;
            {var subQ0=sQuery(id+"F0.wireOp",EDGE,"E0.right");var subQ3=sQuery(id+"F0.wireOp",EDGE,"E0.bottom");Q0=makeQuery(id+"F9.boolean.opBoolean","SPLIT",FACE,{"disambiguationData":[TD([makeQuery(id+"F1.opExtrude","SWEPT_FACE",FACE,{"disambiguationData":[OSD([subQ0])]})])],"derivedFrom":makeQuery(id+"F1.opExtrude","SWEPT_FACE",FACE,{"disambiguationData":[OSD([subQ3])]})});}
            var sketch = newSketch(context, id + "F23", { "sketchPlane" : qUnion([Q0])});
            skLineSegment(sketch, "E78", {"start": v(35.2, -2) * mm, "end": v(35.2, -23) * mm});
            skLineSegment(sketch, "E79", {"start": v(35.2, -23) * mm, "end": v(52.56, -23) * mm});
            skLineSegment(sketch, "E80", {"start": v(35.2, -2) * mm, "end": v(52.56, -2) * mm});
            skLineSegment(sketch, "E81", {"start": v(52.56, -2) * mm, "end": v(48.42, -12.5) * mm});
            skPoint(sketch, "E81.endSnap0", {"position": v(35.2, -12.5) * mm});
            skLineSegment(sketch, "E82", {"start": v(48.42, -12.5) * mm, "end": v(52.56, -23) * mm});
            skLineSegment(sketch, "E83", {"start": v(7.36, -2) * mm, "end": v(24.8, -2) * mm});
            skLineSegment(sketch, "E84", {"start": v(24.8, -23) * mm, "end": v(7.36, -23) * mm});
            skLineSegment(sketch, "E85", {"start": v(7.36, -23) * mm, "end": v(11.5, -12.5) * mm});
            skPoint(sketch, "E85.endSnap0", {"position": v(34, -12.5) * mm});
            skLineSegment(sketch, "E86", {"start": v(11.5, -12.5) * mm, "end": v(7.36, -2) * mm});
            skLineSegment(sketch, "E87", {"start": v(24.8, -2) * mm, "end": v(24.8, -23) * mm});
            skLineSegment(sketch, "E88", {"start": v(-7.42, -2) * mm, "end": v(-11.55, -12.5) * mm});
            skLineSegment(sketch, "E89", {"start": v(-11.55, -12.5) * mm, "end": v(-7.42, -23) * mm});
            skLineSegment(sketch, "E90", {"start": v(-7.42, -23) * mm, "end": v(-14.46, -23) * mm});
            skLineSegment(sketch, "E91", {"start": v(-14.46, -23) * mm, "end": v(-14.46, -2) * mm});
            skLineSegment(sketch, "E92", {"start": v(-14.46, -2) * mm, "end": v(-7.42, -2) * mm});
            skSolve(sketch);
        }
        {
            var Q0;
            Q0 = qSketchRegion(id + "F23", true);
            extrude(context, id + "F24", {"entities" : qUnion([Q0]), "operationType" : NewBodyOperationType.REMOVE, "oppositeDirection" : true, "depth" : 30.25 * mm, "offsetDistance" : 25 * mm, "hasSecondDirection" : true, "secondDirectionOppositeDirection" : true, "secondDirectionDepth" : 8E-4000 * mm});
        }
        {
            var Q0;
            {var subQ0=sQuery(id+"F0.wireOp",EDGE,"E0.right");var subQ3=sQuery(id+"F0.wireOp",EDGE,"E0.bottom");Q0=makeQuery(id+"F9.boolean.opBoolean","SPLIT",FACE,{"disambiguationData":[TD([makeQuery(id+"F1.opExtrude","SWEPT_FACE",FACE,{"disambiguationData":[OSD([subQ0])]})])],"derivedFrom":makeQuery(id+"F1.opExtrude","SWEPT_FACE",FACE,{"disambiguationData":[OSD([subQ3])]})});}
            var sketch = newSketch(context, id + "F25", { "sketchPlane" : qUnion([Q0])});
            skLineSegment(sketch, "E93", {"start": v(65.6, -1.8) * mm, "end": v(73.83, -1.8) * mm});
            skLineSegment(sketch, "E94", {"start": v(73.83, -1.8) * mm, "end": v(73.83, -11.74) * mm});
            skLineSegment(sketch, "E95", {"start": v(65.6, -23.81) * mm, "end": v(73.83, -23.81) * mm});
            skLineSegment(sketch, "E96", {"start": v(73.83, -23.81) * mm, "end": v(73.83, -13.15) * mm});
            skLineSegment(sketch, "E97", {"start": v(65.6, -1.8) * mm, "end": v(70.11, -7.6) * mm});
            skLineSegment(sketch, "E98", {"start": v(70.11, -7.6) * mm, "end": v(71.16, -11.74) * mm});
            skLineSegment(sketch, "E99", {"start": v(71.16, -11.74) * mm, "end": v(70.11, -15.91) * mm});
            skLineSegment(sketch, "E100", {"start": v(70.11, -15.91) * mm, "end": v(65.6, -23.81) * mm});
            skLineSegment(sketch, "E101", {"start": v(73.83, -13.15) * mm, "end": v(73.83, -11.74) * mm});
            skSolve(sketch);
        }
        {
            var Q0;
            Q0 = qSketchRegion(id + "F25", true);
            extrude(context, id + "F26", {"entities" : qUnion([Q0]), "operationType" : NewBodyOperationType.REMOVE, "oppositeDirection" : true, "depth" : 15.4 * mm, "offsetDistance" : 25 * mm, "hasSecondDirection" : true, "secondDirectionOppositeDirection" : true, "secondDirectionDepth" : 6E-4000 * mm});
        }
        {
            var Q0;
            Q0 = qSketchRegion(id + "F25", true);
            extrude(context, id + "F27", {"entities" : qUnion([Q0]), "operationType" : NewBodyOperationType.REMOVE, "oppositeDirection" : true, "depth" : 59 * mm, "offsetDistance" : 25 * mm, "hasSecondDirection" : true, "secondDirectionOppositeDirection" : true, "secondDirectionDepth" : 19.2 * mm});
        }
        {
            var Q0;
            {var subQ0=sQuery(id+"F0.wireOp",EDGE,"E0.right");var subQ3=sQuery(id+"F0.wireOp",EDGE,"E0.bottom");Q0=makeQuery(id+"F9.boolean.opBoolean","SPLIT",FACE,{"disambiguationData":[TD([makeQuery(id+"F1.opExtrude","SWEPT_FACE",FACE,{"disambiguationData":[OSD([subQ0])]})])],"derivedFrom":makeQuery(id+"F1.opExtrude","SWEPT_FACE",FACE,{"disambiguationData":[OSD([subQ3])]})});}
            var sketch = newSketch(context, id + "F28", { "sketchPlane" : qUnion([Q0])});
            skLineSegment(sketch, "E102", {"start": v(47.18, -24) * mm, "end": v(54.52, -24) * mm});
            skLineSegment(sketch, "E103", {"start": v(54.52, -24) * mm, "end": v(49.14, -16.22) * mm});
            skLineSegment(sketch, "E104", {"start": v(49.14, -16.22) * mm, "end": v(49.14, -9.07) * mm});
            skLineSegment(sketch, "E105", {"start": v(49.14, -9.07) * mm, "end": v(54.5, -1.3) * mm});
            skLineSegment(sketch, "E106", {"start": v(54.5, -1.3) * mm, "end": v(47.18, -1.3) * mm});
            skLineSegment(sketch, "E107", {"start": v(47.18, -1.3) * mm, "end": v(47.18, -24) * mm});
            skPoint(sketch, "E108", {"position": v(54.5, 0) * mm});
            skSolve(sketch);
        }
        {
            var Q0;
            Q0 = qSketchRegion(id + "F28", true);
            extrude(context, id + "F29", {"entities" : qUnion([Q0]), "operationType" : NewBodyOperationType.REMOVE, "oppositeDirection" : true, "depth" : 59.1 * mm, "offsetDistance" : 25 * mm, "hasSecondDirection" : true, "secondDirectionOppositeDirection" : true, "secondDirectionDepth" : 45.6 * mm});
        }
        {
            var Q0;
            Q0 = qSketchRegion(id + "F28", true);
            extrude(context, id + "F30", {"entities" : qUnion([Q0]), "operationType" : NewBodyOperationType.REMOVE, "oppositeDirection" : true, "depth" : 41.2 * mm, "offsetDistance" : 25 * mm, "hasSecondDirection" : true, "secondDirectionOppositeDirection" : true, "secondDirectionDepth" : 30.25 * mm});
        }
        {
            var Q0;
            Q0=makeQuery(id+"F28.imprint","IMPRINT",FACE,{"disambiguationData":[TD([[makeQuery(id+"F28.imprint","IMPRINT",EDGE,{"derivedFrom":sQuery(id+"F28.wireOp",EDGE,"E102")}),-1.0]])]});
            var sketch = newSketch(context, id + "F31", { "sketchPlane" : qUnion([Q0])});
            skLineSegment(sketch, "E109.bottom", {"start": v(26, -23.92) * mm, "end": v(34, -23.92) * mm});
            skLineSegment(sketch, "E109.top", {"start": v(26, -1.22) * mm, "end": v(34, -1.22) * mm});
            skLineSegment(sketch, "E109.left", {"start": v(26, -23.92) * mm, "end": v(26, -1.22) * mm});
            skLineSegment(sketch, "E109.right", {"start": v(34, -23.92) * mm, "end": v(34, -1.22) * mm});
            skSolve(sketch);
        }
        {
            var Q0;
            Q0 = qSketchRegion(id + "F31", true);
            extrude(context, id + "F32", {"entities" : qUnion([Q0]), "operationType" : NewBodyOperationType.REMOVE, "oppositeDirection" : true, "depth" : 59 * mm, "offsetDistance" : 25 * mm, "hasSecondDirection" : true, "secondDirectionOppositeDirection" : true, "secondDirectionDepth" : 19.1 * mm});
        }
        {
            var Q0;
            Q0=makeQuery(id+"F1.opExtrude","CAP_FACE",FACE,{"disambiguationData":[OSD([sQuery(id+"F0.wireOp",EDGE,"E0.bottom"),sQuery(id+"F0.wireOp",EDGE,"E0.top"),sQuery(id+"F0.wireOp",EDGE,"E0.left"),sQuery(id+"F0.wireOp",EDGE,"E0.right")])],"isStart":true});
            var sketch = newSketch(context, id + "F33", { "sketchPlane" : qUnion([Q0])});
            skPoint(sketch, "E110.centerSnap0", {"position": v(-30, 20.1) * mm});
            skLineSegment(sketch, "E111.bottom", {"start": v(-73.79, 37.4) * mm, "end": v(-69.79, 37.4) * mm});
            skLineSegment(sketch, "E111.top", {"start": v(-73.79, 23.77) * mm, "end": v(-69.79, 23.77) * mm});
            skLineSegment(sketch, "E111.left", {"start": v(-73.79, 37.4) * mm, "end": v(-73.79, 23.77) * mm});
            skLineSegment(sketch, "E111.right", {"start": v(-69.79, 37.4) * mm, "end": v(-69.79, 23.77) * mm});
            skLineSegment(sketch, "E112.bottom", {"start": v(-73.79, -8.42) * mm, "end": v(-69.79, -8.42) * mm});
            skLineSegment(sketch, "E112.top", {"start": v(-73.79, -16.54) * mm, "end": v(-69.79, -16.54) * mm});
            skLineSegment(sketch, "E112.left", {"start": v(-73.79, -8.42) * mm, "end": v(-73.79, -16.54) * mm});
            skLineSegment(sketch, "E112.right", {"start": v(-69.79, -8.42) * mm, "end": v(-69.79, -16.54) * mm});
            skLineSegment(sketch, "E113.bottom", {"start": v(21.57, -12.17) * mm, "end": v(39.05, -12.17) * mm});
            skLineSegment(sketch, "E113.top", {"start": v(21.57, -16.7) * mm, "end": v(39.05, -16.7) * mm});
            skLineSegment(sketch, "E113.left", {"start": v(21.57, -12.17) * mm, "end": v(21.57, -16.7) * mm});
            skLineSegment(sketch, "E113.right", {"start": v(39.05, -12.17) * mm, "end": v(39.05, -16.7) * mm});
            skLineSegment(sketch, "E114.bottom", {"start": v(-27.43, -1) * mm, "end": v(-32.75, -1) * mm});
            skLineSegment(sketch, "E114.top", {"start": v(-27.43, -17.6) * mm, "end": v(-32.75, -17.6) * mm});
            skLineSegment(sketch, "E114.left", {"start": v(-27.43, -1) * mm, "end": v(-27.43, -17.6) * mm});
            skLineSegment(sketch, "E114.right", {"start": v(-32.75, -1) * mm, "end": v(-32.75, -17.6) * mm});
            skLineSegment(sketch, "E115.bottom", {"start": v(-17.05, 17.47) * mm, "end": v(-13.05, 17.47) * mm});
            skLineSegment(sketch, "E115.top", {"start": v(-17.05, 32.47) * mm, "end": v(-13.05, 32.47) * mm});
            skLineSegment(sketch, "E115.left", {"start": v(-17.05, 17.47) * mm, "end": v(-17.05, 32.47) * mm});
            skLineSegment(sketch, "E115.right", {"start": v(-13.05, 17.47) * mm, "end": v(-13.05, 32.47) * mm});
            skLineSegment(sketch, "E116.bottom", {"start": v(8.41, 27.62) * mm, "end": v(12.41, 27.62) * mm});
            skLineSegment(sketch, "E116.top", {"start": v(8.41, 12.62) * mm, "end": v(12.41, 12.62) * mm});
            skLineSegment(sketch, "E116.left", {"start": v(8.41, 27.62) * mm, "end": v(8.41, 12.62) * mm});
            skLineSegment(sketch, "E116.right", {"start": v(12.41, 27.62) * mm, "end": v(12.41, 12.62) * mm});
            skSolve(sketch);
        }
        {
            var Q0;
            Q0 = qSketchRegion(id + "F33", true);
            extrude(context, id + "F34", {"entities" : qUnion([Q0]), "operationType" : NewBodyOperationType.REMOVE, "oppositeDirection" : true, "depth" : 4.2 * mm, "offsetDistance" : 25 * mm});
        }
        {
            var Q0;
            {var subQ0=sQuery(id+"F0.wireOp",EDGE,"E0.right");var subQ2=sQuery(id+"F0.wireOp",EDGE,"E0.top");Q0=makeQuery(id+"F9.boolean.opBoolean","SPLIT",FACE,{"disambiguationData":[TD([makeQuery(id+"F1.opExtrude","SWEPT_FACE",FACE,{"disambiguationData":[OSD([subQ0])]})])],"derivedFrom":makeQuery(id+"F1.opExtrude","SWEPT_FACE",FACE,{"disambiguationData":[OSD([subQ2])]})});}
            var sketch = newSketch(context, id + "F35", { "sketchPlane" : qUnion([Q0])});
            skLineSegment(sketch, "E117", {"start": v(47.18, 24) * mm, "end": v(54.52, 24) * mm});
            skLineSegment(sketch, "E118", {"start": v(54.52, 24) * mm, "end": v(47.18, 13.38) * mm});
            skLineSegment(sketch, "E119", {"start": v(47.18, 13.38) * mm, "end": v(47.18, 24) * mm});
            skLineSegment(sketch, "E120", {"start": v(47.18, 1.3) * mm, "end": v(54.5, 1.3) * mm});
            skLineSegment(sketch, "E121", {"start": v(54.5, 1.3) * mm, "end": v(47.18, 11.9) * mm});
            skLineSegment(sketch, "E122", {"start": v(47.18, 11.9) * mm, "end": v(47.18, 1.3) * mm});
            skSolve(sketch);
        }
        {
            var Q0;
            Q0 = qSketchRegion(id + "F35", true);
            extrude(context, id + "F36", {"entities" : qUnion([Q0]), "operationType" : NewBodyOperationType.REMOVE, "oppositeDirection" : true, "depth" : 5.1 * mm, "offsetDistance" : 25 * mm});
        }
    });
